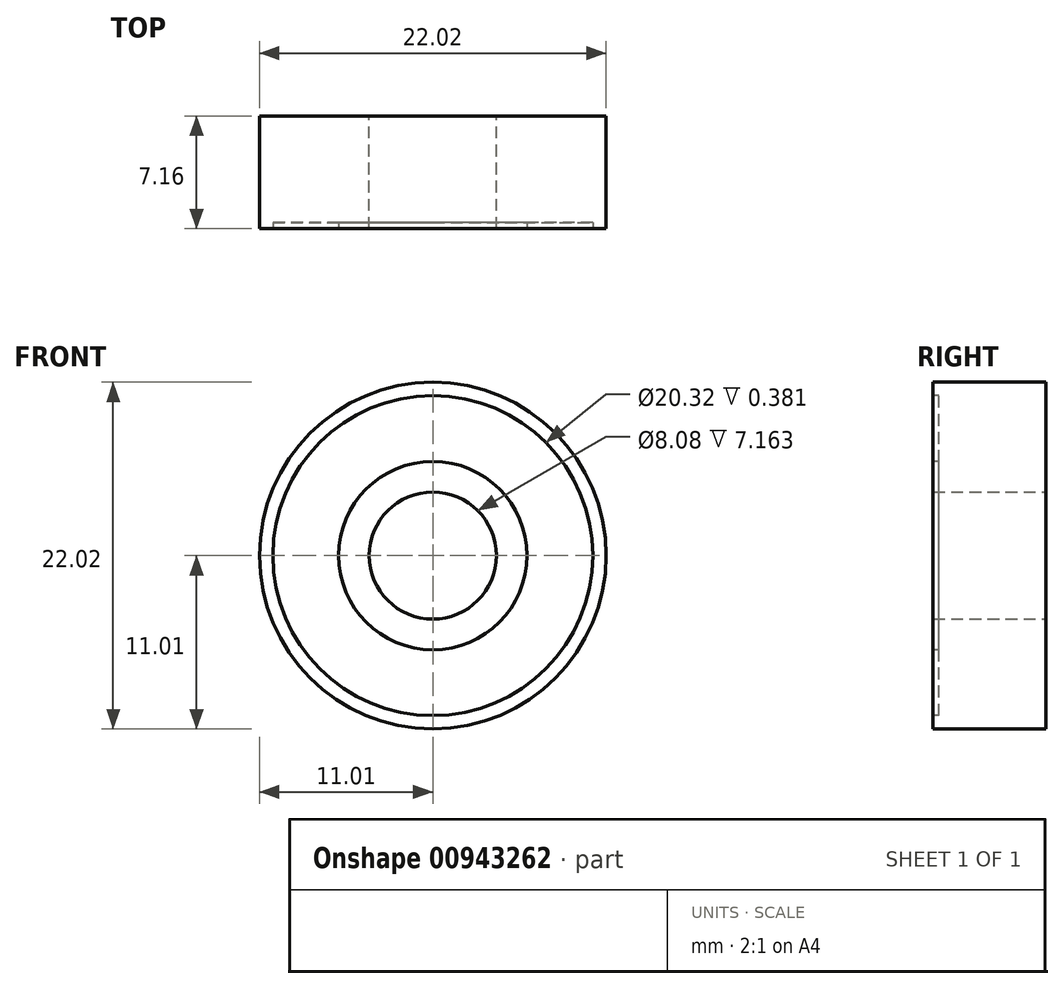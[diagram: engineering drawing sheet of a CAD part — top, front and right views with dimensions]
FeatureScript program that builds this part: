
annotation { "Feature Type Name" : "Feature", "Feature Type Description" : "" }
export const myFeature = defineFeature(function(context is Context, id is Id, definition is map)
    precondition{}
    {
        {
            var Q0;
            Q0=qCreatedBy(makeId("Front.planeOp"),FACE);
            var sketch = newSketch(context, id + "F0", { "sketchPlane" : qUnion([Q0])});
            skCircle(sketch, "E0", {"center": v(0, 0) * mm, "radius": 11.01 * mm});
            skCircle(sketch, "E1", {"center": v(0, 0) * mm, "radius": 5.97 * mm});
            skSolve(sketch);
        }
        {
            var Q0;
            Q0 = qSketchRegion(id + "F0", true);
            extrude(context, id + "F1", {"entities" : qUnion([Q0]), "endBound" : BoundingType.SYMMETRIC, "depth" : 7.16 * mm, "offsetDistance" : 25.4 * mm});
        }
        {
            var Q0;
            Q0=makeQuery(id+"F1.opExtrude","CAP_FACE",FACE,{"disambiguationData":[OSD([sQuery(id+"F0.wireOp",EDGE,"E0"),sQuery(id+"F0.wireOp",EDGE,"E1")])],"isStart":false});
            var sketch = newSketch(context, id + "F2", { "sketchPlane" : qUnion([Q0])});
            skCircle(sketch, "E2", {"center": v(0, 0) * mm, "radius": 5.98 * mm});
            skCircle(sketch, "E3", {"center": v(0, 0) * mm, "radius": 10.16 * mm});
            skSolve(sketch);
        }
        {
            var Q0;
            Q0 = qSketchRegion(id + "F2", true);
            extrude(context, id + "F3", {"entities" : qUnion([Q0]), "operationType" : NewBodyOperationType.REMOVE, "oppositeDirection" : true, "depth" : 0.38 * mm, "offsetDistance" : 25.4 * mm});
        }
        {
            var Q0;
            Q0=qCreatedBy(makeId("Front.planeOp"),FACE);
            var sketch = newSketch(context, id + "F4", { "sketchPlane" : qUnion([Q0])});
            skCircle(sketch, "E4", {"center": v(0, 0) * mm, "radius": 5.97 * mm});
            skCircle(sketch, "E5", {"center": v(0, 0) * mm, "radius": 4.04 * mm});
            skSolve(sketch);
        }
        {
            var Q0;
            Q0 = qSketchRegion(id + "F4", true);
            extrude(context, id + "F5", {"entities" : qUnion([Q0]), "operationType" : NewBodyOperationType.ADD, "endBound" : BoundingType.SYMMETRIC, "depth" : 7.16 * mm, "offsetDistance" : 25.4 * mm});
        }
    });
